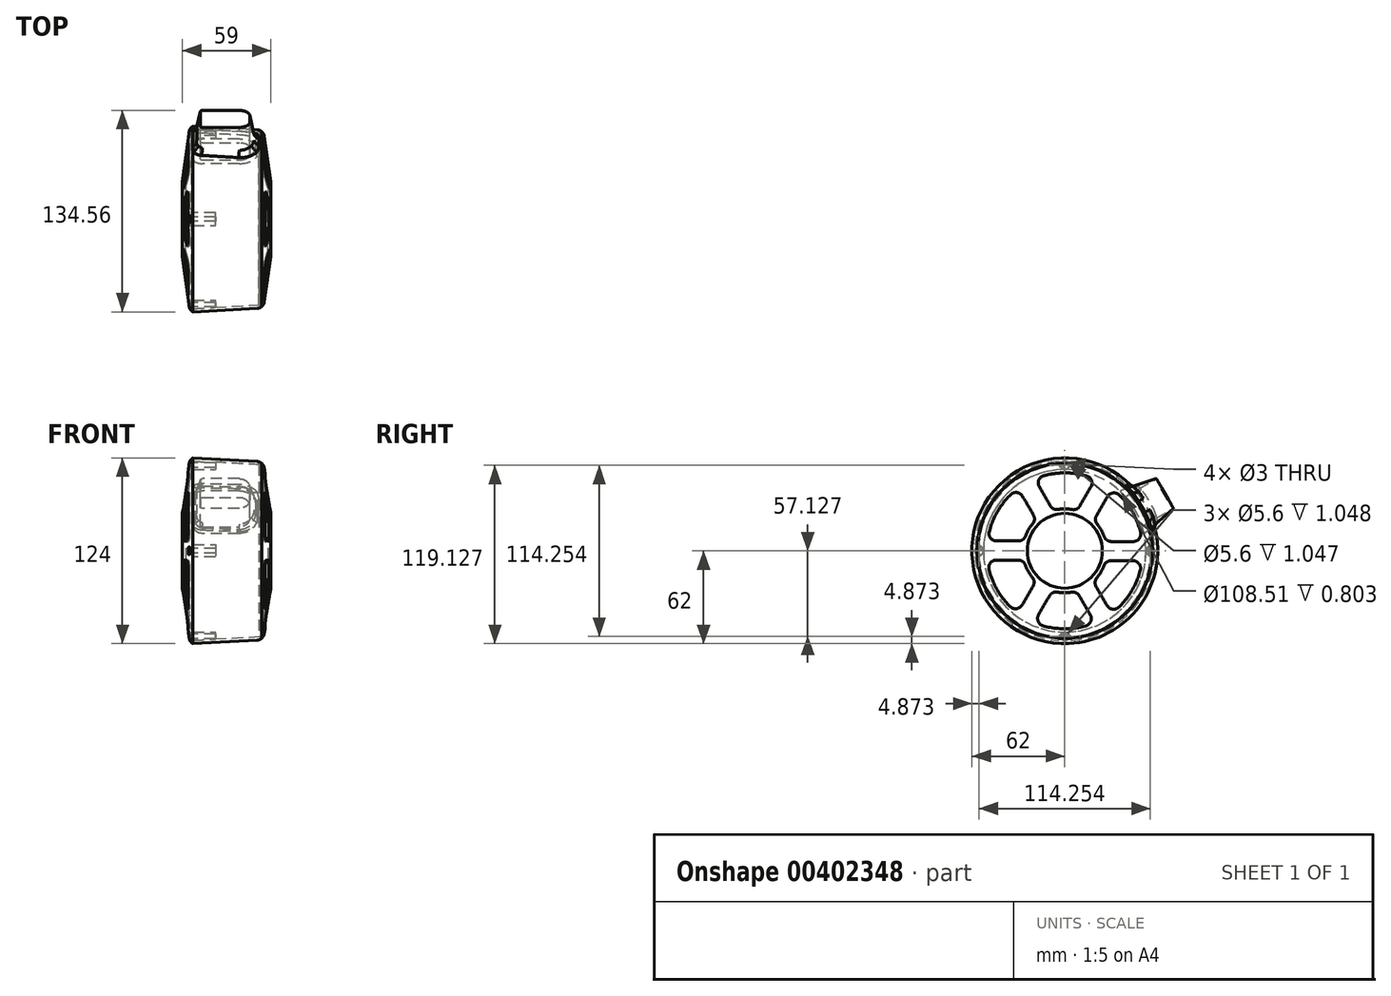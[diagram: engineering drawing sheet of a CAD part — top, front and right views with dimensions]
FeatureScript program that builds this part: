
annotation { "Feature Type Name" : "Feature", "Feature Type Description" : "" }
export const myFeature = defineFeature(function(context is Context, id is Id, definition is map)
    precondition{}
    {
        {
            var Q0;
            Q0=qCreatedBy(makeId("Front.planeOp"),FACE);
            var sketch = newSketch(context, id + "F0", { "sketchPlane" : qUnion([Q0])});
            skPoint(sketch, "E0", {"position": v(47, 59.4) * mm});
            skPoint(sketch, "E1", {"position": v(0, 62) * mm});
            skPoint(sketch, "E2", {"position": v(0, 60) * mm});
            skPoint(sketch, "E3", {"position": v(45, 57.5) * mm});
            skLineSegment(sketch, "E4", {"start": v(-15.88, 0) * mm, "end": v(18.4, 0) * mm, "construction": true});
            skLineSegment(sketch, "E5", {"start": v(0, 14.6) * mm, "end": v(0, -14.84) * mm, "construction": true});
            skLineSegment(sketch, "E6", {"start": v(0, 62) * mm, "end": v(0, 60) * mm});
            skLineSegment(sketch, "E7", {"start": v(45, 57.5) * mm, "end": v(0, 60) * mm});
            skLineSegment(sketch, "E8", {"start": v(47, 59.4) * mm, "end": v(0, 62) * mm});
            skPoint(sketch, "E9", {"position": v(0, 0) * mm});
            skPoint(sketch, "E10", {"position": v(45, 0) * mm});
            skLineSegment(sketch, "E11", {"start": v(45, 57.5) * mm, "end": v(50, 25) * mm});
            skLineSegment(sketch, "E12", {"start": v(50, 25) * mm, "end": v(50, 0) * mm});
            skPoint(sketch, "E13", {"position": v(52, 0) * mm});
            skPoint(sketch, "E14", {"position": v(50, 0) * mm});
            skLineSegment(sketch, "E15", {"start": v(52, 0) * mm, "end": v(50, 0) * mm});
            skLineSegment(sketch, "E16", {"start": v(52, 0) * mm, "end": v(52, 25) * mm});
            skLineSegment(sketch, "E17", {"start": v(52, 25) * mm, "end": v(47, 59.4) * mm});
            skSolve(sketch);
        }
        {
            var Q0;
            Q0=qSketchRegion(id+"F0",true);
            var Q1;
            Q1=sQuery(id+"F0.wireOp",EDGE,"E4");
            revolve(context, id + "F1", {"entities" : qUnion([Q0]), "axis" : qUnion([Q1]), "revolveType" : RevolveType.FULL});
        }
        {
            var Q0;
            Q0=makeQuery(id+"F1.opRevolve","SWEPT_FACE",FACE,{"disambiguationData":[OSD([sQuery(id+"F0.wireOp",EDGE,"E6")])]});
            cPlane(context, id + "F2", {"entities" : qUnion([Q0]), "cplaneType" : CPlaneType.OFFSET, "offset" : 0 * mm, "width" : 150 * mm, "height" : 150 * mm});
        }
        {
            var Q0;
            Q0=qCreatedBy(id+"F2.planeOp",FACE);
            var sketch = newSketch(context, id + "F3", { "sketchPlane" : qUnion([Q0])});
            skPoint(sketch, "E18", {"position": v(0, 60) * mm});
            skEllipticalArc(sketch, "E19", {});
            skArc(sketch, "E20.0", {"start": v(4.24, 59.85) * mm, "mid": v(0, 60) * mm, "end": v(-4.24, 59.85) * mm});
            skPoint(sketch, "E21", {"position": v(0, 57.13) * mm});
            skCircle(sketch, "E22", {"center": v(0, 57.13) * mm, "radius": 1.5 * mm});
            skEllipticalArc(sketch, "E23.1.0", {});
            skArc(sketch, "E23.1.1", {"start": v(-59.85, 4.24) * mm, "mid": v(-60, 0) * mm, "end": v(-59.85, -4.24) * mm});
            skCircle(sketch, "E23.1.2", {"center": v(-57.13, 0) * mm, "radius": 1.5 * mm});
            skEllipticalArc(sketch, "E23.2.0", {});
            skArc(sketch, "E23.2.1", {"start": v(-4.24, -59.85) * mm, "mid": v(0, -60) * mm, "end": v(4.24, -59.85) * mm});
            skCircle(sketch, "E23.2.2", {"center": v(0, -57.13) * mm, "radius": 1.5 * mm});
            skEllipticalArc(sketch, "E23.3.0", {});
            skArc(sketch, "E23.3.1", {"start": v(59.85, -4.24) * mm, "mid": v(60, 0) * mm, "end": v(59.85, 4.24) * mm});
            skCircle(sketch, "E23.3.2", {"center": v(57.13, 0) * mm, "radius": 1.5 * mm});
            const initialGuessF3  = {"E19": [0, 0.06, 0, -1, 0.0057459472492984815, 0.004242868250736747, 4.738514968524078, 1.544670338655507], "E23.1.0": [-0.06, 0, 1, 0, 0.0057459472492984815, 0.004242868250736747, 4.738514968524078, 1.544670338655507], "E23.2.0": [0, -0.06, 0, 1, 0.0057459472492984815, 0.004242868250736747, 4.738514968524078, 1.544670338655507], "E23.3.0": [0.06, 0, -1, 0, 0.0057459472492984815, 0.004242868250736747, 4.738514968524078, 1.544670338655507]};
            skSetInitialGuess(sketch, initialGuessF3);
            skSolve(sketch);
        }
        {
            var Q0;
            Q0=qSketchRegion(id+"F3",true);
            extrude(context, id + "F4", {"entities" : qUnion([Q0]), "operationType" : NewBodyOperationType.ADD, "oppositeDirection" : true, "depth" : 15 * mm});
        }
        {
            var Q0;
            Q0=qCreatedBy(makeId("Front.planeOp"),FACE);
            var sketch = newSketch(context, id + "F5", { "sketchPlane" : qUnion([Q0])});
            skLineSegment(sketch, "E24.0", {"start": v(0, -62) * mm, "end": v(0, 62) * mm, "construction": true});
            skLineSegment(sketch, "E25.0", {"start": v(0, 4.24) * mm, "end": v(0, 59.85) * mm, "construction": true});
            skPoint(sketch, "E26", {"position": v(0, 62) * mm});
            skPoint(sketch, "E27", {"position": v(0, 59.85) * mm});
            skLineSegment(sketch, "E28", {"start": v(0, 62) * mm, "end": v(-2, 62) * mm, "construction": true});
            skPoint(sketch, "E29", {"position": v(-2, 62) * mm});
            skLineSegment(sketch, "E30.0", {"start": v(52, -25) * mm, "end": v(52, 25) * mm, "construction": true});
            skLineSegment(sketch, "E31", {"start": v(52, 25) * mm, "end": v(0, 25) * mm, "construction": true});
            skLineSegment(sketch, "E32", {"start": v(-52.04, 0) * mm, "end": v(63.38, 0) * mm, "construction": true});
            skLineSegment(sketch, "E33.0", {"start": v(0, 59.85) * mm, "end": v(0, 54.25) * mm, "construction": true});
            skPoint(sketch, "E34", {"position": v(0, 54.25) * mm});
            skLineSegment(sketch, "E35.0", {"start": v(47, -59.4) * mm, "end": v(47, 59.4) * mm, "construction": true});
            skPoint(sketch, "E36", {"position": v(47, 25) * mm});
            skPoint(sketch, "E37", {"position": v(52, 25) * mm});
            skPoint(sketch, "E38", {"position": v(0, 25) * mm});
            skPoint(sketch, "E39", {"position": v(-7, 25) * mm});
            skLineSegment(sketch, "E40", {"start": v(-7, 25) * mm, "end": v(-7, 0) * mm});
            skLineSegment(sketch, "E41", {"start": v(-2, 62) * mm, "end": v(-7, 25) * mm});
            skLineSegment(sketch, "E42", {"start": v(-2, 62) * mm, "end": v(0, 62) * mm});
            skLineSegment(sketch, "E43", {"start": v(0, 54.25) * mm, "end": v(0, 62) * mm});
            skLineSegment(sketch, "E44", {"start": v(-7, 0) * mm, "end": v(-5, 0) * mm});
            skLineSegment(sketch, "E45", {"start": v(-5, 0) * mm, "end": v(-5, 25) * mm});
            skLineSegment(sketch, "E46", {"start": v(-5, 25) * mm, "end": v(-0.8, 54.25) * mm});
            skLineSegment(sketch, "E47", {"start": v(0, 54.25) * mm, "end": v(-0.8, 54.25) * mm});
            skPoint(sketch, "E48", {"position": v(-0.8, 54.25) * mm});
            skSolve(sketch);
        }
        {
            var Q0;
            Q0=qSketchRegion(id+"F5",true);
            var Q1;
            Q1=sQuery(id+"F5.wireOp",EDGE,"E32");
            revolve(context, id + "F6", {"entities" : qUnion([Q0]), "axis" : qUnion([Q1]), "revolveType" : RevolveType.FULL});
        }
        {
            var Q0;
            Q0=makeQuery(id+"F1.opRevolve","SWEPT_EDGE",EDGE,{"disambiguationData":[OSD([sQuery(id+"F0.wireOp",EDGE,"E8"),sQuery(id+"F0.wireOp",EDGE,"E17")])]});
            var Q1;
            Q1=makeQuery(id+"F6.opRevolve","SWEPT_EDGE",EDGE,{"disambiguationData":[OSD([sQuery(id+"F5.wireOp",EDGE,"E41"),sQuery(id+"F5.wireOp",EDGE,"E42")])]});
            fillet(context, id + "F7", {"entities" : qUnion([Q0, Q1]), "radius" : 5 * mm, "tangentPropagation" : true, "allowEdgeOverflow" : false});
        }
        {
            var Q0;
            Q0=makeQuery(id+"F1.opRevolve","SWEPT_FACE",FACE,{"disambiguationData":[OSD([sQuery(id+"F0.wireOp",EDGE,"E16")])]});
            cPlane(context, id + "F8", {"entities" : qUnion([Q0]), "cplaneType" : CPlaneType.OFFSET, "offset" : 0 * mm, "width" : 150 * mm, "height" : 150 * mm});
        }
        {
            var Q0;
            Q0=qCreatedBy(id+"F8.planeOp",FACE);
            var sketch = newSketch(context, id + "F9", { "sketchPlane" : qUnion([Q0])});
            skArc(sketch, "E49.0", {"start": v(-4.58, 27.62) * mm, "mid": v(0.18, 28) * mm, "end": v(4.93, 27.56) * mm});
            skArc(sketch, "E50.0", {"start": v(14.54, 50) * mm, "mid": v(0.22, 52.06) * mm, "end": v(-14.1, 50.12) * mm});
            skLineSegment(sketch, "E51", {"start": v(-9.72, 30.06) * mm, "end": v(-17.08, 42.8) * mm});
            skLineSegment(sketch, "E52", {"start": v(17.48, 42.7) * mm, "end": v(10.14, 29.99) * mm});
            skLineSegment(sketch, "E53", {"start": v(0, 9.44) * mm, "end": v(0, 28) * mm, "construction": true});
            skPoint(sketch, "E54", {"position": v(-20.1, 48.04) * mm});
            skPoint(sketch, "E55", {"position": v(20.48, 47.9) * mm});
            skPoint(sketch, "E56", {"position": v(-7.88, 26.87) * mm});
            skPoint(sketch, "E57", {"position": v(8.27, 26.75) * mm});
            skLineSegment(sketch, "E58.trimOffspring", {"start": v(0, 52.06) * mm, "end": v(0, 66.14) * mm, "construction": true});
            skArc(sketch, "E59.filletArc", {"start": v(17.48, 42.7) * mm, "mid": v(17.79, 47.07) * mm, "end": v(14.54, 50) * mm});
            skArc(sketch, "E60.filletArc", {"start": v(-14.1, 50.12) * mm, "mid": v(-17.38, 47.2) * mm, "end": v(-17.08, 42.8) * mm});
            skArc(sketch, "E61.filletArc", {"start": v(-9.72, 30.06) * mm, "mid": v(-7.53, 28.04) * mm, "end": v(-4.58, 27.62) * mm});
            skArc(sketch, "E62.filletArc", {"start": v(4.93, 27.56) * mm, "mid": v(7.91, 27.95) * mm, "end": v(10.14, 29.99) * mm});
            skArc(sketch, "E63.1.0", {"start": v(-36.04, 37.6) * mm, "mid": v(-44.97, 26.22) * mm, "end": v(-50.46, 12.85) * mm});
            skArc(sketch, "E63.1.1", {"start": v(-28.24, 36.49) * mm, "mid": v(-31.87, 38.94) * mm, "end": v(-36.04, 37.6) * mm});
            skLineSegment(sketch, "E63.1.2", {"start": v(-28.24, 36.49) * mm, "end": v(-20.9, 23.77) * mm});
            skArc(sketch, "E63.1.3", {"start": v(-21.4, 18.05) * mm, "mid": v(-20.25, 20.83) * mm, "end": v(-20.9, 23.77) * mm});
            skArc(sketch, "E63.1.4", {"start": v(-26.21, 9.85) * mm, "mid": v(-24.16, 14.15) * mm, "end": v(-21.4, 18.05) * mm});
            skArc(sketch, "E63.1.5", {"start": v(-30.9, 6.6) * mm, "mid": v(-28.04, 7.5) * mm, "end": v(-26.21, 9.85) * mm});
            skLineSegment(sketch, "E63.1.6", {"start": v(-30.9, 6.6) * mm, "end": v(-45.61, 6.6) * mm});
            skArc(sketch, "E63.1.7", {"start": v(-50.46, 12.85) * mm, "mid": v(-49.56, 8.54) * mm, "end": v(-45.61, 6.6) * mm});
            skArc(sketch, "E63.2.0", {"start": v(-50.58, -12.42) * mm, "mid": v(-45.2, -25.84) * mm, "end": v(-36.35, -37.27) * mm});
            skArc(sketch, "E63.2.1", {"start": v(-45.72, -6.22) * mm, "mid": v(-49.66, -8.13) * mm, "end": v(-50.58, -12.42) * mm});
            skLineSegment(sketch, "E63.2.2", {"start": v(-45.72, -6.22) * mm, "end": v(-31.04, -6.22) * mm});
            skArc(sketch, "E63.2.3", {"start": v(-26.33, -9.52) * mm, "mid": v(-28.16, -7.12) * mm, "end": v(-31.04, -6.22) * mm});
            skArc(sketch, "E63.2.4", {"start": v(-21.63, -17.78) * mm, "mid": v(-24.34, -13.85) * mm, "end": v(-26.33, -9.52) * mm});
            skArc(sketch, "E63.2.5", {"start": v(-21.17, -23.45) * mm, "mid": v(-20.51, -20.54) * mm, "end": v(-21.63, -17.78) * mm});
            skLineSegment(sketch, "E63.2.6", {"start": v(-21.17, -23.45) * mm, "end": v(-28.53, -36.2) * mm});
            skArc(sketch, "E63.2.7", {"start": v(-36.35, -37.27) * mm, "mid": v(-32.18, -38.65) * mm, "end": v(-28.53, -36.2) * mm});
            skArc(sketch, "E63.3.0", {"start": v(-14.54, -50) * mm, "mid": v(-0.22, -52.06) * mm, "end": v(14.1, -50.12) * mm});
            skArc(sketch, "E63.3.1", {"start": v(-17.48, -42.7) * mm, "mid": v(-17.79, -47.07) * mm, "end": v(-14.54, -50) * mm});
            skLineSegment(sketch, "E63.3.2", {"start": v(-17.48, -42.7) * mm, "end": v(-10.14, -29.99) * mm});
            skArc(sketch, "E63.3.3", {"start": v(-4.93, -27.56) * mm, "mid": v(-7.91, -27.95) * mm, "end": v(-10.14, -29.99) * mm});
            skArc(sketch, "E63.3.4", {"start": v(4.58, -27.62) * mm, "mid": v(-0.18, -28) * mm, "end": v(-4.93, -27.56) * mm});
            skArc(sketch, "E63.3.5", {"start": v(9.72, -30.06) * mm, "mid": v(7.53, -28.04) * mm, "end": v(4.58, -27.62) * mm});
            skLineSegment(sketch, "E63.3.6", {"start": v(9.72, -30.06) * mm, "end": v(17.08, -42.8) * mm});
            skArc(sketch, "E63.3.7", {"start": v(14.1, -50.12) * mm, "mid": v(17.38, -47.2) * mm, "end": v(17.08, -42.8) * mm});
            skArc(sketch, "E63.4.0", {"start": v(36.04, -37.6) * mm, "mid": v(44.97, -26.22) * mm, "end": v(50.46, -12.85) * mm});
            skArc(sketch, "E63.4.1", {"start": v(28.24, -36.49) * mm, "mid": v(31.87, -38.94) * mm, "end": v(36.04, -37.6) * mm});
            skLineSegment(sketch, "E63.4.2", {"start": v(28.24, -36.49) * mm, "end": v(20.9, -23.77) * mm});
            skArc(sketch, "E63.4.3", {"start": v(21.4, -18.05) * mm, "mid": v(20.25, -20.83) * mm, "end": v(20.9, -23.77) * mm});
            skArc(sketch, "E63.4.4", {"start": v(26.21, -9.85) * mm, "mid": v(24.16, -14.15) * mm, "end": v(21.4, -18.05) * mm});
            skArc(sketch, "E63.4.5", {"start": v(30.9, -6.6) * mm, "mid": v(28.04, -7.5) * mm, "end": v(26.21, -9.85) * mm});
            skLineSegment(sketch, "E63.4.6", {"start": v(30.9, -6.6) * mm, "end": v(45.61, -6.6) * mm});
            skArc(sketch, "E63.4.7", {"start": v(50.46, -12.85) * mm, "mid": v(49.56, -8.54) * mm, "end": v(45.61, -6.6) * mm});
            skArc(sketch, "E63.5.0", {"start": v(50.58, 12.42) * mm, "mid": v(45.2, 25.84) * mm, "end": v(36.35, 37.27) * mm});
            skArc(sketch, "E63.5.1", {"start": v(45.72, 6.22) * mm, "mid": v(49.66, 8.13) * mm, "end": v(50.58, 12.42) * mm});
            skLineSegment(sketch, "E63.5.2", {"start": v(45.72, 6.22) * mm, "end": v(31.04, 6.22) * mm});
            skArc(sketch, "E63.5.3", {"start": v(26.33, 9.52) * mm, "mid": v(28.16, 7.12) * mm, "end": v(31.04, 6.22) * mm});
            skArc(sketch, "E63.5.4", {"start": v(21.63, 17.78) * mm, "mid": v(24.34, 13.85) * mm, "end": v(26.33, 9.52) * mm});
            skArc(sketch, "E63.5.5", {"start": v(21.17, 23.45) * mm, "mid": v(20.51, 20.54) * mm, "end": v(21.63, 17.78) * mm});
            skLineSegment(sketch, "E63.5.6", {"start": v(21.17, 23.45) * mm, "end": v(28.53, 36.2) * mm});
            skArc(sketch, "E63.5.7", {"start": v(36.35, 37.27) * mm, "mid": v(32.18, 38.65) * mm, "end": v(28.53, 36.2) * mm});
            skSolve(sketch);
        }
        {
            var Q0;
            Q0=qSketchRegion(id+"F9",true);
            extrude(context, id + "F10", {"entities" : qUnion([Q0]), "operationType" : NewBodyOperationType.REMOVE, "oppositeDirection" : true, "depth" : 88 * mm});
        }
        {
            var Q0;
            Q0=qCreatedBy(makeId("Front.planeOp"),FACE);
            var sketch = newSketch(context, id + "F11", { "sketchPlane" : qUnion([Q0])});
            skLineSegment(sketch, "E64.0.0", {"start": v(52, 0) * mm, "end": v(52, 25) * mm, "construction": true});
            skLineSegment(sketch, "E64.0.1", {"start": v(52, 25) * mm, "end": v(47, 59.4) * mm, "construction": true});
            skLineSegment(sketch, "E64.0.2", {"start": v(47, 59.4) * mm, "end": v(0, 62) * mm, "construction": true});
            skLineSegment(sketch, "E64.0.3", {"start": v(0, 62) * mm, "end": v(0, 60) * mm, "construction": true});
            skLineSegment(sketch, "E64.0.4", {"start": v(0, 60) * mm, "end": v(40.95, 57.72) * mm, "construction": true});
            skLineSegment(sketch, "E64.0.5", {"start": v(45.62, 53.5) * mm, "end": v(50, 25) * mm, "construction": true});
            skLineSegment(sketch, "E64.0.6", {"start": v(50, 25) * mm, "end": v(50, 0) * mm, "construction": true});
            skLineSegment(sketch, "E64.0.7", {"start": v(50, 0) * mm, "end": v(52, 0) * mm, "construction": true});
            skPoint(sketch, "E65", {"position": v(0, 61) * mm});
            skPoint(sketch, "E66", {"position": v(51, 0) * mm});
            skPoint(sketch, "E67", {"position": v(50, 25) * mm});
            skPoint(sketch, "E68", {"position": v(52, 25) * mm});
            skLineSegment(sketch, "E69", {"start": v(52, 25) * mm, "end": v(50, 25) * mm, "construction": true});
            skPoint(sketch, "E70", {"position": v(51, 25) * mm});
            skLineSegment(sketch, "E71", {"start": v(47, 59.4) * mm, "end": v(45, 57.5) * mm, "construction": true});
            skPoint(sketch, "E72", {"position": v(46, 58.45) * mm});
            skLineSegment(sketch, "E73", {"start": v(0, 61) * mm, "end": v(46, 58.45) * mm});
            skLineSegment(sketch, "E74", {"start": v(46, 58.45) * mm, "end": v(51, 25) * mm});
            skLineSegment(sketch, "E75", {"start": v(51, 25) * mm, "end": v(51, 0) * mm});
            skLineSegment(sketch, "E76", {"start": v(51, 0) * mm, "end": v(50, 0) * mm});
            skLineSegment(sketch, "E77", {"start": v(50, 0) * mm, "end": v(50, 25) * mm});
            skLineSegment(sketch, "E78", {"start": v(50, 25) * mm, "end": v(45, 57.5) * mm});
            skLineSegment(sketch, "E79", {"start": v(45, 57.5) * mm, "end": v(0, 60) * mm});
            skLineSegment(sketch, "E80", {"start": v(0, 60) * mm, "end": v(0, 61) * mm});
            skPoint(sketch, "E81.visualSharp", {"position": v(45, 57.5) * mm});
            skSolve(sketch);
        }
        {
            var Q0;
            Q0=qSketchRegion(id+"F11",true);
            var Q1;
            Q1=sQuery(id+"F0.wireOp",EDGE,"E4");
            revolve(context, id + "F12", {"operationType" : NewBodyOperationType.ADD, "entities" : qUnion([Q0]), "axis" : qUnion([Q1]), "revolveType" : RevolveType.FULL});
        }
        {
            var Q0;
            Q0=qCreatedBy(makeId("Front.planeOp"),FACE);
            var sketch = newSketch(context, id + "F13", { "sketchPlane" : qUnion([Q0])});
            skLineSegment(sketch, "E82.0.0", {"start": v(-0.8, 54.25) * mm, "end": v(0, 54.25) * mm, "construction": true});
            skLineSegment(sketch, "E82.0.1", {"start": v(0, 54.25) * mm, "end": v(0, 62) * mm, "construction": true});
            skLineSegment(sketch, "E82.0.2", {"start": v(0, 62) * mm, "end": v(-2, 62) * mm, "construction": true});
            skLineSegment(sketch, "E82.0.3", {"start": v(-2, 62) * mm, "end": v(-7, 25) * mm, "construction": true});
            skLineSegment(sketch, "E82.0.4", {"start": v(-7, 25) * mm, "end": v(-7, 0) * mm, "construction": true});
            skLineSegment(sketch, "E82.0.5", {"start": v(-7, 0) * mm, "end": v(-5, 0) * mm, "construction": true});
            skLineSegment(sketch, "E82.0.6", {"start": v(-5, 0) * mm, "end": v(-5, 25) * mm, "construction": true});
            skLineSegment(sketch, "E82.0.7", {"start": v(-5, 25) * mm, "end": v(-0.8, 54.25) * mm, "construction": true});
            skPoint(sketch, "E83", {"position": v(-0.8, 54.25) * mm});
            skPoint(sketch, "E84", {"position": v(-5, 25) * mm});
            skPoint(sketch, "E85", {"position": v(-7, 25) * mm});
            skPoint(sketch, "E86", {"position": v(-2, 62) * mm});
            skPoint(sketch, "E87", {"position": v(-5, 0) * mm});
            skPoint(sketch, "E88", {"position": v(-7, 0) * mm});
            skPoint(sketch, "E89", {"position": v(0, 62) * mm});
            skPoint(sketch, "E90", {"position": v(0, 60.4) * mm});
            skPoint(sketch, "E91", {"position": v(0, 57) * mm});
            skPoint(sketch, "E92", {"position": v(0, 54.25) * mm});
            skLineSegment(sketch, "E93", {"start": v(-0.8, 54.25) * mm, "end": v(-5, 25) * mm});
            skLineSegment(sketch, "E94", {"start": v(-5, 25) * mm, "end": v(-7, 25) * mm, "construction": true});
            skPoint(sketch, "E95", {"position": v(-6, 25) * mm});
            skLineSegment(sketch, "E96.0", {"start": v(-0.02, 61.73) * mm, "end": v(-5.02, 24.73) * mm, "construction": true});
            skLineSegment(sketch, "E97", {"start": v(-0.8, 54.25) * mm, "end": v(-3.05, 54.25) * mm, "construction": true});
            skPoint(sketch, "E98", {"position": v(-1.03, 54.25) * mm});
            skPoint(sketch, "E99", {"position": v(-1.92, 54.25) * mm});
            skLineSegment(sketch, "E100", {"start": v(-0.8, 54.25) * mm, "end": v(-1.92, 54.25) * mm});
            skLineSegment(sketch, "E101", {"start": v(-1.92, 54.25) * mm, "end": v(-6, 25) * mm});
            skLineSegment(sketch, "E102", {"start": v(-6, 25) * mm, "end": v(-5, 25) * mm});
            skSolve(sketch);
        }
        {
            var Q0;
            Q0=qSketchRegion(id+"F13",true);
            var Q1;
            Q1=sQuery(id+"F5.wireOp",EDGE,"E32");
            revolve(context, id + "F14", {"operationType" : NewBodyOperationType.ADD, "entities" : qUnion([Q0]), "axis" : qUnion([Q1]), "revolveType" : RevolveType.FULL});
        }
        {
            var Q0;
            Q0=qCreatedBy(makeId("Right.planeOp"),FACE);
            cPlane(context, id + "F15", {"entities" : qUnion([Q0]), "cplaneType" : CPlaneType.OFFSET, "offset" : 2 * mm, "oppositeDirection" : true, "width" : 150 * mm, "height" : 150 * mm});
        }
        {
            var Q0;
            Q0=qCreatedBy(id+"F15.planeOp",FACE);
            var sketch = newSketch(context, id + "F16", { "sketchPlane" : qUnion([Q0])});
            skPoint(sketch, "E103", {"position": v(0, 57.13) * mm});
            skPoint(sketch, "E104", {"position": v(-57.13, 0) * mm});
            skPoint(sketch, "E105", {"position": v(57.13, 0) * mm});
            skPoint(sketch, "E106", {"position": v(0, -57.13) * mm});
            skCircle(sketch, "E107", {"center": v(0, 57.13) * mm, "radius": 1.5 * mm});
            skCircle(sketch, "E108", {"center": v(-57.13, 0) * mm, "radius": 1.5 * mm});
            skCircle(sketch, "E109", {"center": v(0, -57.13) * mm, "radius": 1.5 * mm});
            skCircle(sketch, "E110", {"center": v(57.13, 0) * mm, "radius": 1.5 * mm});
            skSolve(sketch);
        }
        {
            var Q0;
            Q0=qSketchRegion(id+"F16",true);
            extrude(context, id + "F17", {"entities" : qUnion([Q0]), "operationType" : NewBodyOperationType.REMOVE, "endBound" : BoundingType.SYMMETRIC, "depth" : 25 * mm});
        }
        {
            var Q0;
            Q0=makeQuery(id+"F6.opRevolve","SWEPT_FACE",FACE,{"disambiguationData":[OSD([sQuery(id+"F5.wireOp",EDGE,"E40")])]});
            cPlane(context, id + "F18", {"entities" : qUnion([Q0]), "cplaneType" : CPlaneType.OFFSET, "offset" : 0 * mm, "width" : 150 * mm, "height" : 150 * mm});
        }
        {
            var Q0;
            Q0=qCreatedBy(id+"F18.planeOp",FACE);
            var sketch = newSketch(context, id + "F19", { "sketchPlane" : qUnion([Q0])});
            skArc(sketch, "E111.0", {"start": v(58.3, 0.93) * mm, "mid": v(41.23, 41.23) * mm, "end": v(0.93, 58.3) * mm, "construction": true});
            skArc(sketch, "E112.0", {"start": v(-0.93, 58.3) * mm, "mid": v(-41.23, 41.23) * mm, "end": v(-58.3, 0.93) * mm, "construction": true});
            skCircle(sketch, "E113.0", {"center": v(0, 57.13) * mm, "radius": 1.5 * mm, "construction": true});
            skCircle(sketch, "E114", {"center": v(0, 57.13) * mm, "radius": 2.8 * mm});
            skCircle(sketch, "E115.1.0", {"center": v(-57.13, 0) * mm, "radius": 2.8 * mm});
            skCircle(sketch, "E115.2.0", {"center": v(0, -57.13) * mm, "radius": 2.8 * mm});
            skCircle(sketch, "E115.3.0", {"center": v(57.13, 0) * mm, "radius": 2.8 * mm});
            skSolve(sketch);
        }
        {
            var Q0;
            Q0=qSketchRegion(id+"F19",true);
            extrude(context, id + "F20", {"entities" : qUnion([Q0]), "operationType" : NewBodyOperationType.REMOVE, "oppositeDirection" : true, "depth" : 5 * mm});
        }
        {
            var Q0;
            Q0=qCreatedBy(makeId("Origin.pointOp"),VERTEX);
            var Q1;
            Q1=makeQuery(id+"F1.opRevolve","SWEPT_FACE",FACE,{"disambiguationData":[OSD([sQuery(id+"F0.wireOp",EDGE,"E12")])]});
            cPlane(context, id + "F21", {"entities" : qUnion([Q0, Q1]), "cplaneType" : CPlaneType.PLANE_POINT, "offset" : 25 * mm, "width" : 150 * mm, "height" : 150 * mm});
        }
        {
            var Q0;
            Q0=qCreatedBy(makeId("Front.planeOp"),FACE);
            var sketch = newSketch(context, id + "F22", { "sketchPlane" : qUnion([Q0])});
            skLineSegment(sketch, "E116", {"start": v(0, 73.4) * mm, "end": v(0, -47.52) * mm, "construction": true});
            skLineSegment(sketch, "E117", {"start": v(-76.26, 0) * mm, "end": v(95.72, 0) * mm, "construction": true});
            skLineSegment(sketch, "E118.0", {"start": v(50, 25) * mm, "end": v(50, 0) * mm, "construction": true});
            skLineSegment(sketch, "E118.1", {"start": v(45, 57.5) * mm, "end": v(50, 25) * mm, "construction": true});
            skLineSegment(sketch, "E118.2", {"start": v(45, 57.5) * mm, "end": v(0, 60) * mm, "construction": true});
            skPoint(sketch, "E118.3", {"position": v(47.5, 41.25) * mm});
            skLineSegment(sketch, "E119", {"start": v(45, 57.5) * mm, "end": v(45, -16.08) * mm, "construction": true});
            skLineSegment(sketch, "E120", {"start": v(44, 68.03) * mm, "end": v(44, -16.35) * mm, "construction": true});
            skPoint(sketch, "E121", {"position": v(44, 57.56) * mm});
            skPoint(sketch, "E122", {"position": v(50, 0) * mm});
            skPoint(sketch, "E123", {"position": v(44, 0) * mm});
            skLineSegment(sketch, "E124", {"start": v(44, 57.56) * mm, "end": v(45, 57.5) * mm});
            skLineSegment(sketch, "E125", {"start": v(45, 57.5) * mm, "end": v(50, 25) * mm});
            skLineSegment(sketch, "E126", {"start": v(50, 25) * mm, "end": v(50, 0) * mm});
            skLineSegment(sketch, "E127", {"start": v(50, 0) * mm, "end": v(44, 0) * mm});
            skLineSegment(sketch, "E128", {"start": v(44, 0) * mm, "end": v(44, 57.56) * mm});
            skSolve(sketch);
        }
        {
            var Q0;
            Q0=qSketchRegion(id+"F22",true);
            var Q1;
            Q1=sQuery(id+"F22.wireOp",EDGE,"E117");
            revolve(context, id + "F23", {"entities" : qUnion([Q0]), "axis" : qUnion([Q1]), "revolveType" : RevolveType.FULL});
        }
        {
            var Q0;
            Q0=makeQuery(id+"F23.opRevolve","SWEPT_FACE",FACE,{"disambiguationData":[OSD([sQuery(id+"F22.wireOp",EDGE,"E128")])]});
            cPlane(context, id + "F24", {"entities" : qUnion([Q0]), "cplaneType" : CPlaneType.OFFSET, "offset" : 0 * mm, "width" : 150 * mm, "height" : 150 * mm});
        }
        {
            var Q0;
            Q0=qCreatedBy(id+"F24.planeOp",FACE);
            var sketch = newSketch(context, id + "F25", { "sketchPlane" : qUnion([Q0])});
            skArc(sketch, "E129.0.0", {"start": v(-50.58, 12.42) * mm, "mid": v(-45.2, 25.84) * mm, "end": v(-36.35, 37.27) * mm, "construction": true});
            skArc(sketch, "E129.0.1", {"start": v(-36.35, 37.27) * mm, "mid": v(-32.18, 38.65) * mm, "end": v(-28.53, 36.2) * mm, "construction": true});
            skFitSpline(sketch, "E129.0.2", {"points": [v(-28.53, 36.2) * mm, v(-26.08, 31.95) * mm, v(-23.62, 27.7) * mm, v(-21.17, 23.45) * mm], "construction": true});
            skArc(sketch, "E129.0.3", {"start": v(-21.17, 23.45) * mm, "mid": v(-20.51, 20.54) * mm, "end": v(-21.63, 17.78) * mm, "construction": true});
            skArc(sketch, "E129.0.4", {"start": v(-26.33, 9.52) * mm, "mid": v(-24.34, 13.85) * mm, "end": v(-21.63, 17.78) * mm, "construction": true});
            skArc(sketch, "E129.0.5", {"start": v(-26.33, 9.52) * mm, "mid": v(-28.16, 7.12) * mm, "end": v(-31.04, 6.22) * mm, "construction": true});
            skFitSpline(sketch, "E129.0.6", {"points": [v(-31.04, 6.22) * mm, v(-35.93, 6.22) * mm, v(-40.83, 6.22) * mm, v(-45.72, 6.22) * mm], "construction": true});
            skArc(sketch, "E129.0.7", {"start": v(-45.72, 6.22) * mm, "mid": v(-49.66, 8.13) * mm, "end": v(-50.58, 12.42) * mm, "construction": true});
            skPoint(sketch, "E130", {"position": v(-45.2, 25.84) * mm});
            skPoint(sketch, "E131", {"position": v(-24.34, 13.85) * mm});
            skLineSegment(sketch, "E132", {"start": v(0.24, -0.16) * mm, "end": v(-45.2, 25.84) * mm, "construction": true});
            skLineSegment(sketch, "E133", {"start": v(0, 0) * mm, "end": v(0, 43.28) * mm, "construction": true});
            skSolve(sketch);
        }
        {
            var Q0;
            Q0=sQuery(id+"F25.wireOp",EDGE,"E129.0.0");
            cPoint(context, id + "F26", {"entities" : qUnion([Q0]), "parameter" : 0.5});
        }
        {
            var Q0;
            Q0=sQuery(id+"F25.wireOp",EDGE,"E132");
            var Q1;
            Q1 = qCreatedBy(id + "F26" ,VERTEX);
            cPlane(context, id + "F27", {"entities" : qUnion([Q0, Q1]), "cplaneType" : CPlaneType.LINE_POINT, "offset" : 25 * mm, "width" : 150 * mm, "height" : 150 * mm});
        }
        {
            var Q0;
            Q0=qCreatedBy(id+"F27.planeOp",FACE);
            var sketch = newSketch(context, id + "F28", { "sketchPlane" : qUnion([Q0])});
            skPoint(sketch, "E134.0", {"position": v(-44, -0.02) * mm});
            skFitSpline(sketch, "E135.0.0", {"points": [v(-46.95, -14.34) * mm, v(-46.95, -13.17) * mm, v(-46.95, -10.81) * mm, v(-46.95, -7.83) * mm, v(-46.95, -5.43) * mm, v(-46.95, -3.6) * mm, v(-46.95, -1.79) * mm, v(-46.95, 0.63) * mm, v(-46.95, 3.64) * mm, v(-46.95, 8.41) * mm, v(-46.95, 11.96) * mm, v(-46.95, 14.3) * mm], "construction": true});
            skFitSpline(sketch, "E135.0.1", {"points": [v(-46.95, 14.3) * mm, v(-46.95, 14.67) * mm, v(-46.96, 15.2) * mm, v(-47, 15.85) * mm, v(-47.02, 16.3) * mm, v(-47.06, 16.7) * mm, v(-47.12, 17.16) * mm, v(-47.26, 17.8) * mm, v(-47.45, 18.03) * mm, v(-47.68, 17.75) * mm, v(-47.8, 17.44) * mm, v(-47.85, 17.25) * mm], "construction": true});
            skFitSpline(sketch, "E135.0.2", {"points": [v(-47.85, 17.25) * mm, v(-48.57, 14.78) * mm, v(-49.3, 12.31) * mm, v(-50.01, 9.84) * mm], "construction": true});
            skFitSpline(sketch, "E135.0.3", {"points": [v(-50.01, 9.84) * mm, v(-50.05, 9.71) * mm, v(-50.12, 9.43) * mm, v(-50.23, 8.9) * mm, v(-50.32, 8.32) * mm, v(-50.4, 7.65) * mm, v(-50.45, 7.06) * mm, v(-50.49, 6.57) * mm, v(-50.52, 6.07) * mm, v(-50.54, 5.44) * mm, v(-50.55, 4.94) * mm, v(-50.55, 4.68) * mm], "construction": true});
            skLineSegment(sketch, "E135.0.4", {"start": v(-50.55, -4.82) * mm, "end": v(-50.55, 4.68) * mm, "construction": true});
            skFitSpline(sketch, "E135.0.5", {"points": [v(-50.55, -4.82) * mm, v(-50.55, -5.07) * mm, v(-50.54, -5.59) * mm, v(-50.51, -6.36) * mm, v(-50.46, -7.1) * mm, v(-50.4, -7.83) * mm, v(-50.31, -8.49) * mm, v(-50.19, -9.3) * mm, v(-50.08, -9.76) * mm, v(-50, -10.02) * mm], "construction": true});
            skFitSpline(sketch, "E135.0.6", {"points": [v(-50, -10.02) * mm, v(-49.29, -12.45) * mm, v(-48.56, -14.88) * mm, v(-47.84, -17.31) * mm], "construction": true});
            skFitSpline(sketch, "E135.0.7", {"points": [v(-47.84, -17.31) * mm, v(-47.73, -17.69) * mm, v(-47.56, -18.02) * mm, v(-47.35, -17.95) * mm, v(-47.21, -17.65) * mm, v(-47.12, -17.2) * mm, v(-47.06, -16.72) * mm, v(-47.02, -16.33) * mm, v(-46.99, -15.88) * mm, v(-46.96, -15.23) * mm, v(-46.95, -14.7) * mm, v(-46.95, -14.34) * mm], "construction": true});
            skPoint(sketch, "E136", {"position": v(-46.95, -0.02) * mm});
            skLineSegment(sketch, "E137", {"start": v(-44, -0.02) * mm, "end": v(34.52, -0.02) * mm, "construction": true});
            skLineSegment(sketch, "E138.bottom", {"start": v(-30.9, 11.38) * mm, "end": v(-6.25, 11.38) * mm});
            skLineSegment(sketch, "E138.top", {"start": v(-30.9, -11.42) * mm, "end": v(-6.25, -11.42) * mm});
            skLineSegment(sketch, "E138.left", {"start": v(-37.9, 4.38) * mm, "end": v(-37.9, -4.42) * mm});
            skLineSegment(sketch, "E138.right", {"start": v(-5, 10.13) * mm, "end": v(-5, -10.17) * mm});
            skPoint(sketch, "E138.middle", {"position": v(-21.45, -0.02) * mm});
            skPoint(sketch, "E139.visualSharp", {"position": v(-5, 11.38) * mm});
            skArc(sketch, "E139.filletArc", {"start": v(-5, 10.13) * mm, "mid": v(-5.37, 11.01) * mm, "end": v(-6.25, 11.38) * mm});
            skPoint(sketch, "E140.visualSharp", {"position": v(-5, -11.42) * mm});
            skArc(sketch, "E140.filletArc", {"start": v(-6.25, -11.42) * mm, "mid": v(-5.37, -11.05) * mm, "end": v(-5, -10.17) * mm});
            skPoint(sketch, "E141.visualSharp", {"position": v(-37.9, 11.38) * mm});
            skArc(sketch, "E141.filletArc", {"start": v(-30.9, 11.38) * mm, "mid": v(-35.85, 9.33) * mm, "end": v(-37.9, 4.38) * mm});
            skPoint(sketch, "E142.visualSharp", {"position": v(-37.9, -11.42) * mm});
            skArc(sketch, "E142.filletArc", {"start": v(-37.9, -4.42) * mm, "mid": v(-35.85, -9.37) * mm, "end": v(-30.9, -11.42) * mm});
            skLineSegment(sketch, "E143.0", {"start": v(-42.92, 59.62) * mm, "end": v(-42.92, -59.62) * mm, "construction": true});
            skLineSegment(sketch, "E144.0", {"start": v(0, 62) * mm, "end": v(0, -62) * mm, "construction": true});
            skSolve(sketch);
        }
        {
            var Q0;
            Q0 = qSketchRegion(id + "F28", true);
            extrude(context, id + "F29", {"entities" : qUnion([Q0]), "operationType" : NewBodyOperationType.REMOVE, "depth" : 25 * mm});
        }
        {
            var Q0;
            Q0=sQuery(id+"F25.wireOp",EDGE,"E132");
            cPlane(context, id + "F30", {"entities" : qUnion([Q0]), "cplaneType" : CPlaneType.LINE_ANGLE, "offset" : 25 * mm, "angle" : 90 * degree, "width" : 150 * mm, "height" : 150 * mm});
        }
        {
            var Q0;
            Q0=qCreatedBy(id+"F27.planeOp",FACE);
            cPlane(context, id + "F31", {"entities" : qUnion([Q0]), "cplaneType" : CPlaneType.OFFSET, "offset" : 25 * mm, "width" : 150 * mm, "height" : 150 * mm});
        }
        {
            var Q0;
            Q0=qCreatedBy(id+"F27.planeOp",FACE);
            var sketch = newSketch(context, id + "F32", { "sketchPlane" : qUnion([Q0])});
            skArc(sketch, "E145.0", {"start": v(-30.9, -16.42) * mm, "mid": v(-39.39, -12.9) * mm, "end": v(-42.9, -4.42) * mm});
            skLineSegment(sketch, "E145.1", {"start": v(-42.9, 4.38) * mm, "end": v(-42.9, -4.42) * mm});
            skFitSpline(sketch, "E145.2", {"points": [v(-30.9, -16.42) * mm, v(-22.68, -16.42) * mm, v(-14.47, -16.42) * mm, v(-6.25, -16.42) * mm]});
            skArc(sketch, "E145.3", {"start": v(-42.9, 4.38) * mm, "mid": v(-39.39, 12.86) * mm, "end": v(-30.9, 16.38) * mm});
            skArc(sketch, "E145.4", {"start": v(0, -10.17) * mm, "mid": v(-1.83, -14.6) * mm, "end": v(-6.25, -16.42) * mm});
            skLineSegment(sketch, "E145.5", {"start": v(0, 10.13) * mm, "end": v(0, -10.17) * mm});
            skArc(sketch, "E145.6", {"start": v(-6.25, 16.38) * mm, "mid": v(-1.83, 14.55) * mm, "end": v(0, 10.13) * mm});
            skFitSpline(sketch, "E145.7", {"points": [v(-30.9, 16.38) * mm, v(-22.68, 16.38) * mm, v(-14.47, 16.38) * mm, v(-6.25, 16.38) * mm]});
            skFitSpline(sketch, "E146.0", {"points": [v(-30.9, 11.38) * mm, v(-22.68, 11.38) * mm, v(-14.47, 11.38) * mm, v(-6.25, 11.38) * mm], "construction": true});
            skArc(sketch, "E147.0", {"start": v(-6.25, 11.38) * mm, "mid": v(-5.37, 11.01) * mm, "end": v(-5, 10.13) * mm, "construction": true});
            skLineSegment(sketch, "E148.0", {"start": v(-5, 10.13) * mm, "end": v(-5, -10.17) * mm, "construction": true});
            skArc(sketch, "E149.0", {"start": v(-5, -10.17) * mm, "mid": v(-5.37, -11.05) * mm, "end": v(-6.25, -11.42) * mm, "construction": true});
            skFitSpline(sketch, "E150.0", {"points": [v(-30.9, -11.42) * mm, v(-22.68, -11.42) * mm, v(-14.47, -11.42) * mm, v(-6.25, -11.42) * mm], "construction": true});
            skArc(sketch, "E151.0", {"start": v(-30.9, -11.42) * mm, "mid": v(-35.85, -9.37) * mm, "end": v(-37.9, -4.42) * mm, "construction": true});
            skLineSegment(sketch, "E152.0", {"start": v(-37.9, 4.38) * mm, "end": v(-37.9, -4.42) * mm, "construction": true});
            skArc(sketch, "E153.0", {"start": v(-37.9, 4.38) * mm, "mid": v(-35.85, 9.33) * mm, "end": v(-30.9, 11.38) * mm, "construction": true});
            skSolve(sketch);
        }
        {
            var Q0;
            Q0=qCreatedBy(id+"F31.planeOp",FACE);
            var sketch = newSketch(context, id + "F33", { "sketchPlane" : qUnion([Q0])});
            skFitSpline(sketch, "E154.0", {"points": [v(-30.9, 11.38) * mm, v(-22.68, 11.38) * mm, v(-14.47, 11.38) * mm, v(-6.25, 11.38) * mm]});
            skArc(sketch, "E155.0", {"start": v(-37.9, 4.38) * mm, "mid": v(-35.85, 9.33) * mm, "end": v(-30.9, 11.38) * mm});
            skLineSegment(sketch, "E156.0", {"start": v(-37.9, 4.38) * mm, "end": v(-37.9, -4.42) * mm});
            skArc(sketch, "E157.0", {"start": v(-30.9, -11.42) * mm, "mid": v(-35.85, -9.37) * mm, "end": v(-37.9, -4.42) * mm});
            skFitSpline(sketch, "E158.0", {"points": [v(-30.9, -11.42) * mm, v(-22.68, -11.42) * mm, v(-14.47, -11.42) * mm, v(-6.25, -11.42) * mm]});
            skArc(sketch, "E159.0", {"start": v(-5, -10.17) * mm, "mid": v(-5.37, -11.05) * mm, "end": v(-6.25, -11.42) * mm});
            skLineSegment(sketch, "E160.0", {"start": v(-5, 10.13) * mm, "end": v(-5, -10.17) * mm});
            skArc(sketch, "E161.0", {"start": v(-6.25, 11.38) * mm, "mid": v(-5.37, 11.01) * mm, "end": v(-5, 10.13) * mm});
            skSolve(sketch);
        }
        {
            var Q1;
            Q1 = qSketchRegion(id + "F33", true);
            var Q2;
            Q2 = qSketchRegion(id + "F32", true);
            loft(context, id + "F34", {"operationType" : NewBodyOperationType.ADD, "sheetProfilesArray" : [{ "sheetProfileEntities" : qUnion([Q1]) }, { "sheetProfileEntities" : qUnion([Q2]) }]});
        }
        {
            var Q0;
            Q0=makeQuery(id+"F34.boolean.opBoolean","INTERSECT",EDGE,{"derivedFrom":[makeQuery(id+"F1.opRevolve","SWEPT_FACE",FACE,{"disambiguationData":[OSD([sQuery(id+"F0.wireOp",EDGE,"E8")])]}),makeQuery(id+"F34.opLoft","SWEPT_FACE",FACE,{"disambiguationData":[OSD([sQuery(id+"F32.wireOp",EDGE,"E145.0"),sQuery(id+"F32.wireOp",EDGE,"E145.2"),sQuery(id+"F32.wireOp",EDGE,"E145.4"),sQuery(id+"F33.wireOp",EDGE,"E157.0"),sQuery(id+"F33.wireOp",EDGE,"E158.0"),sQuery(id+"F33.wireOp",EDGE,"E159.0")])]})]});
            fillet(context, id + "F35", {"entities" : qUnion([Q0]), "radius" : 5 * mm, "tangentPropagation" : true, "allowEdgeOverflow" : false});
        }
        {
            var Q0;
            Q0=qCreatedBy(id+"F31.planeOp",FACE);
            var sketch = newSketch(context, id + "F36", { "sketchPlane" : qUnion([Q0])});
            skArc(sketch, "E162.0.0", {"start": v(-5, 10.13) * mm, "mid": v(-5.37, 11.01) * mm, "end": v(-6.25, 11.38) * mm});
            skFitSpline(sketch, "E162.0.1", {"points": [v(-6.25, 11.38) * mm, v(-14.47, 11.38) * mm, v(-22.68, 11.38) * mm, v(-30.9, 11.38) * mm]});
            skArc(sketch, "E162.0.2", {"start": v(-30.9, 11.38) * mm, "mid": v(-35.85, 9.33) * mm, "end": v(-37.9, 4.38) * mm});
            skLineSegment(sketch, "E162.0.3", {"start": v(-37.9, -4.42) * mm, "end": v(-37.9, 4.38) * mm});
            skArc(sketch, "E162.0.4", {"start": v(-37.9, -4.42) * mm, "mid": v(-35.85, -9.37) * mm, "end": v(-30.9, -11.42) * mm});
            skFitSpline(sketch, "E162.0.5", {"points": [v(-6.25, -11.42) * mm, v(-14.47, -11.42) * mm, v(-22.68, -11.42) * mm, v(-30.9, -11.42) * mm]});
            skArc(sketch, "E162.0.6", {"start": v(-6.25, -11.42) * mm, "mid": v(-5.37, -11.05) * mm, "end": v(-5, -10.17) * mm});
            skLineSegment(sketch, "E162.0.7", {"start": v(-5, -10.17) * mm, "end": v(-5, 10.13) * mm});
            skSolve(sketch);
        }
        {
            var Q0;
            Q0=makeQuery(id+"F36.imprint","IMPRINT",FACE,{"disambiguationData":[TD([[makeQuery(id+"F36.imprint","IMPRINT",EDGE,{"derivedFrom":sQuery(id+"F36.wireOp",EDGE,"E162.0.0")}),1.0]])]});
            extrude(context, id + "F37", {"entities" : qUnion([Q0]), "operationType" : NewBodyOperationType.REMOVE, "oppositeDirection" : true, "depth" : 40.8 * mm});
        }
    });
